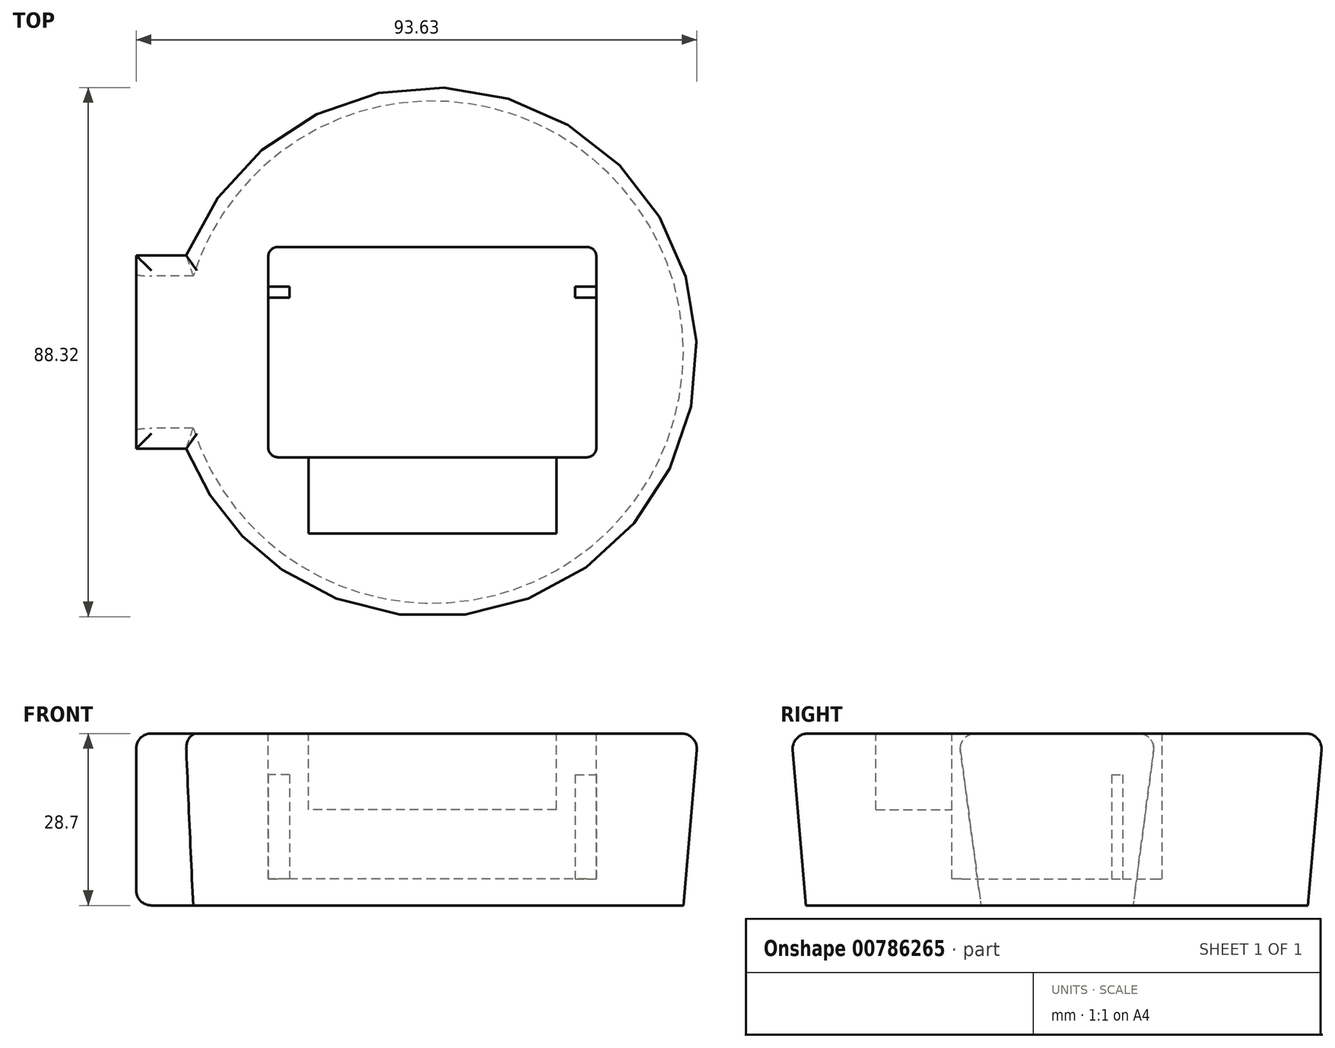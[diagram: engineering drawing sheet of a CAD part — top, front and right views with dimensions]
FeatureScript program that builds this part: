
annotation { "Feature Type Name" : "Feature", "Feature Type Description" : "" }
export const myFeature = defineFeature(function(context is Context, id is Id, definition is map)
    precondition{}
    {
        {
            var Q0;
            Q0=qCreatedBy(makeId("Front.planeOp"),FACE);
            var sketch = newSketch(context, id + "F0", { "sketchPlane" : qUnion([Q0])});
            skLineSegment(sketch, "E0", {"start": v(0, 0) * mm, "end": v(-41.91, 0) * mm});
            skLineSegment(sketch, "E1", {"start": v(-41.91, 0) * mm, "end": v(-44.39, 28.7) * mm});
            skLineSegment(sketch, "E2", {"start": v(-44.39, 28.7) * mm, "end": v(0, 28.7) * mm});
            skLineSegment(sketch, "E3", {"start": v(0, 28.7) * mm, "end": v(0, 0) * mm});
            skSolve(sketch);
        }
        {
            var Q0;
            Q0=makeQuery(id+"F0.imprint","IMPRINT",FACE,{"disambiguationData":[TD([[makeQuery(id+"F0.imprint","IMPRINT",EDGE,{"derivedFrom":sQuery(id+"F0.wireOp",EDGE,"E0")}),-1.0]])]});
            var sketch = newSketch(context, id + "F1", { "sketchPlane" : qUnion([Q0])});
            skLineSegment(sketch, "E4", {"start": v(0, -29.96) * mm, "end": v(0, 103.31) * mm, "construction": true});
            skSolve(sketch);
        }
        {
            var Q0;
            Q0 = qSketchRegion(id + "F0", true);
            var Q1;
            Q1=sQuery(id+"F1.wireOp",EDGE,"E4");
            revolve(context, id + "F2", {"surfaceOperationType" : NewSurfaceOperationType.NEW, "entities" : qUnion([Q0]), "axis" : qUnion([Q1]), "revolveType" : RevolveType.FULL});
        }
        {
            var Q0;
            Q0=makeQuery(id+"F2.opRevolve","SWEPT_FACE",FACE,{"disambiguationData":[OSD([sQuery(id+"F0.wireOp",EDGE,"E2")])]});
            var sketch = newSketch(context, id + "F3", { "sketchPlane" : qUnion([Q0])});
            skLineSegment(sketch, "E5.bottom", {"start": v(0, 16.51) * mm, "end": v(-49.47, 16.51) * mm});
            skLineSegment(sketch, "E5.top", {"start": v(0, -16.51) * mm, "end": v(-49.47, -16.51) * mm});
            skLineSegment(sketch, "E5.left", {"start": v(0, 16.51) * mm, "end": v(0, -16.51) * mm});
            skLineSegment(sketch, "E5.right", {"start": v(-49.47, 16.51) * mm, "end": v(-49.47, -16.51) * mm});
            skPoint(sketch, "E6", {"position": v(0, 0) * mm});
            skSolve(sketch);
        }
        {
            var Q0;
            Q0 = qSketchRegion(id + "F3", true);
            var Q1;
            Q1=makeQuery(id+"F2.opRevolve","SWEPT_FACE",FACE,{"disambiguationData":[OSD([sQuery(id+"F0.wireOp",EDGE,"E0")])]});
            extrude(context, id + "F4", {"entities" : qUnion([Q0]), "operationType" : NewBodyOperationType.ADD, "endBound" : BoundingType.UP_TO_SURFACE, "oppositeDirection" : true, "depth" : 25.4 * mm, "endBoundEntityFace" : qUnion([Q1]), "offsetDistance" : 25.4 * mm});
        }
        {
            var Q0;
            Q0=makeQuery(id+"F4.opExtrude","SWEPT_FACE",FACE,{"disambiguationData":[OSD([sQuery(id+"F3.wireOp",EDGE,"E5.right")])]});
            var sketch = newSketch(context, id + "F5", { "sketchPlane" : qUnion([Q0])});
            skLineSegment(sketch, "E7", {"start": v(-16.51, 28.7) * mm, "end": v(-16.51, 0) * mm});
            skLineSegment(sketch, "E8", {"start": v(-16.51, 0) * mm, "end": v(-12.7, 0) * mm});
            skLineSegment(sketch, "E9", {"start": v(-12.7, 0) * mm, "end": v(-16.51, 28.7) * mm});
            skLineSegment(sketch, "E10", {"start": v(16.5, 28.7) * mm, "end": v(16.5, 0) * mm});
            skLineSegment(sketch, "E11", {"start": v(16.5, 0) * mm, "end": v(12.7, 0) * mm});
            skLineSegment(sketch, "E12", {"start": v(12.7, 0) * mm, "end": v(16.5, 28.7) * mm});
            skSolve(sketch);
        }
        {
            var Q0;
            Q0 = qSketchRegion(id + "F5", true);
            var Q1;
            Q1=makeQuery(id+"F2.opRevolve","SWEPT_FACE",FACE,{"disambiguationData":[OSD([sQuery(id+"F0.wireOp",EDGE,"E1")])]});
            extrude(context, id + "F6", {"entities" : qUnion([Q0]), "operationType" : NewBodyOperationType.REMOVE, "endBound" : BoundingType.UP_TO_SURFACE, "oppositeDirection" : true, "depth" : 25.4 * mm, "endBoundEntityFace" : qUnion([Q1]), "offsetDistance" : 25.4 * mm});
        }
        {
            var Q0;
            Q0=makeQuery(id+"F4.boolean.opBoolean","MERGE",FACE,{"derivedFrom":[makeQuery(id+"F2.opRevolve","SWEPT_FACE",FACE,{"disambiguationData":[OSD([sQuery(id+"F0.wireOp",EDGE,"E2")])]}),makeQuery(id+"F4.opExtrude","CAP_FACE",FACE,{"disambiguationData":[OSD([sQuery(id+"F3.wireOp",EDGE,"E5.bottom"),sQuery(id+"F3.wireOp",EDGE,"E5.top"),sQuery(id+"F3.wireOp",EDGE,"E5.left"),sQuery(id+"F3.wireOp",EDGE,"E5.right")])],"isStart":true})]});
            var sketch = newSketch(context, id + "F7", { "sketchPlane" : qUnion([Q0])});
            skLineSegment(sketch, "E13.bottom", {"start": v(25.8, -17.55) * mm, "end": v(-25.8, -17.55) * mm});
            skLineSegment(sketch, "E13.top", {"start": v(25.8, 17.55) * mm, "end": v(-25.8, 17.55) * mm});
            skLineSegment(sketch, "E13.left", {"start": v(27.4, -15.96) * mm, "end": v(27.4, 15.96) * mm});
            skLineSegment(sketch, "E13.right", {"start": v(-27.4, -15.96) * mm, "end": v(-27.4, 15.96) * mm});
            skPoint(sketch, "E13.middle", {"position": v(0, 0) * mm});
            skPoint(sketch, "E14.visualSharp", {"position": v(-27.4, 17.55) * mm});
            skArc(sketch, "E14.filletArc", {"start": v(-25.8, 17.55) * mm, "mid": v(-26.93, 17.09) * mm, "end": v(-27.4, 15.96) * mm});
            skPoint(sketch, "E15.visualSharp", {"position": v(27.4, 17.55) * mm});
            skArc(sketch, "E15.filletArc", {"start": v(27.4, 15.96) * mm, "mid": v(26.93, 17.09) * mm, "end": v(25.8, 17.55) * mm});
            skPoint(sketch, "E16.visualSharp", {"position": v(27.4, -17.55) * mm});
            skArc(sketch, "E16.filletArc", {"start": v(25.8, -17.55) * mm, "mid": v(26.93, -17.09) * mm, "end": v(27.4, -15.96) * mm});
            skPoint(sketch, "E17.visualSharp", {"position": v(-27.4, -17.55) * mm});
            skArc(sketch, "E17.filletArc", {"start": v(-27.4, -15.96) * mm, "mid": v(-26.93, -17.09) * mm, "end": v(-25.8, -17.55) * mm});
            skSolve(sketch);
        }
        {
            var Q0;
            Q0 = qSketchRegion(id + "F7", true);
            extrude(context, id + "F8", {"entities" : qUnion([Q0]), "operationType" : NewBodyOperationType.REMOVE, "oppositeDirection" : true, "depth" : 24.28 * mm, "offsetDistance" : 25.4 * mm});
        }
        {
            var Q0;
            Q0=makeQuery(id+"F8.boolean.opBoolean","COPY",FACE,{"derivedFrom":makeQuery(id+"F8.opExtrude","CAP_FACE",FACE,{"disambiguationData":[OSD([sQuery(id+"F7.wireOp",EDGE,"E13.bottom"),sQuery(id+"F7.wireOp",EDGE,"E13.top"),sQuery(id+"F7.wireOp",EDGE,"E13.left"),sQuery(id+"F7.wireOp",EDGE,"E13.right"),sQuery(id+"F7.wireOp",EDGE,"E14.filletArc"),sQuery(id+"F7.wireOp",EDGE,"E15.filletArc"),sQuery(id+"F7.wireOp",EDGE,"E16.filletArc"),sQuery(id+"F7.wireOp",EDGE,"E17.filletArc")])],"isStart":false})});
            var sketch = newSketch(context, id + "F9", { "sketchPlane" : qUnion([Q0])});
            skLineSegment(sketch, "E18.bottom", {"start": v(23.84, 9.1) * mm, "end": v(27.4, 9.1) * mm});
            skLineSegment(sketch, "E18.top", {"start": v(23.84, 10.95) * mm, "end": v(27.4, 10.95) * mm});
            skLineSegment(sketch, "E18.left", {"start": v(23.84, 9.1) * mm, "end": v(23.84, 10.95) * mm});
            skLineSegment(sketch, "E18.right", {"start": v(27.4, 9.1) * mm, "end": v(27.4, 10.95) * mm});
            skPoint(sketch, "E18.middle", {"position": v(25.62, 10.02) * mm});
            skLineSegment(sketch, "E19.bottom", {"start": v(-23.84, 9.1) * mm, "end": v(-27.4, 9.1) * mm});
            skLineSegment(sketch, "E19.top", {"start": v(-23.84, 10.95) * mm, "end": v(-27.4, 10.95) * mm});
            skLineSegment(sketch, "E19.left", {"start": v(-23.84, 9.1) * mm, "end": v(-23.84, 10.95) * mm});
            skLineSegment(sketch, "E19.right", {"start": v(-27.4, 9.1) * mm, "end": v(-27.4, 10.95) * mm});
            skPoint(sketch, "E19.middle", {"position": v(-25.62, 10.02) * mm});
            skSolve(sketch);
        }
        {
            var Q0;
            Q0 = qSketchRegion(id + "F9", true);
            extrude(context, id + "F10", {"entities" : qUnion([Q0]), "operationType" : NewBodyOperationType.ADD, "depth" : 17.42 * mm, "offsetDistance" : 25.4 * mm});
        }
        {
            var Q0;
            Q0=makeQuery(id+"F4.boolean.opBoolean","MERGE",FACE,{"derivedFrom":[makeQuery(id+"F2.opRevolve","SWEPT_FACE",FACE,{"disambiguationData":[OSD([sQuery(id+"F0.wireOp",EDGE,"E2")])]}),makeQuery(id+"F4.opExtrude","CAP_FACE",FACE,{"disambiguationData":[OSD([sQuery(id+"F3.wireOp",EDGE,"E5.bottom"),sQuery(id+"F3.wireOp",EDGE,"E5.top"),sQuery(id+"F3.wireOp",EDGE,"E5.left"),sQuery(id+"F3.wireOp",EDGE,"E5.right")])],"isStart":true})]});
            var sketch = newSketch(context, id + "F11", { "sketchPlane" : qUnion([Q0])});
            skLineSegment(sketch, "E20.bottom", {"start": v(20.7, -30.25) * mm, "end": v(-20.7, -30.25) * mm});
            skLineSegment(sketch, "E20.top", {"start": v(20.7, -17.55) * mm, "end": v(-20.7, -17.55) * mm});
            skLineSegment(sketch, "E20.left", {"start": v(20.7, -30.25) * mm, "end": v(20.7, -17.55) * mm});
            skLineSegment(sketch, "E20.right", {"start": v(-20.7, -30.25) * mm, "end": v(-20.7, -17.55) * mm});
            skPoint(sketch, "E20.middle", {"position": v(0, -23.9) * mm});
            skSolve(sketch);
        }
        {
            var Q0;
            Q0 = qSketchRegion(id + "F11", true);
            extrude(context, id + "F12", {"entities" : qUnion([Q0]), "operationType" : NewBodyOperationType.REMOVE, "oppositeDirection" : true, "depth" : 12.7 * mm, "offsetDistance" : 25.4 * mm});
        }
        {
            var Q0;
            Q0=makeQuery(id+"F2.opRevolve","SWEPT_EDGE",EDGE,{"disambiguationData":[OSD([sQuery(id+"F0.wireOp",EDGE,"E1"),sQuery(id+"F0.wireOp",EDGE,"E2")])]});
            var Q1;
            Q1=makeQuery(id+"F6.boolean.opBoolean","MERGE",EDGE,{"derivedFrom":[makeQuery(id+"F4.opExtrude","CAP_EDGE",EDGE,{"disambiguationData":[OSD([sQuery(id+"F3.wireOp",EDGE,"E5.top")])],"isStart":true})],"fromTools":[makeQuery(id+"F6.opExtrude","SWEPT_EDGE",EDGE,{"disambiguationData":[OSD([sQuery(id+"F3.wireOp",EDGE,"E5.right"),sQuery(id+"F5.wireOp",EDGE,"E10"),sQuery(id+"F5.wireOp",EDGE,"E12")])]})]});
            var Q2;
            Q2=makeQuery(id+"F4.opExtrude","CAP_EDGE",EDGE,{"disambiguationData":[OSD([sQuery(id+"F3.wireOp",EDGE,"E5.right")])],"isStart":true});
            var Q3;
            Q3=makeQuery(id+"F6.boolean.opBoolean","MERGE",EDGE,{"derivedFrom":[makeQuery(id+"F4.opExtrude","CAP_EDGE",EDGE,{"disambiguationData":[OSD([sQuery(id+"F3.wireOp",EDGE,"E5.bottom")])],"isStart":true})],"fromTools":[makeQuery(id+"F6.opExtrude","SWEPT_EDGE",EDGE,{"disambiguationData":[OSD([sQuery(id+"F3.wireOp",EDGE,"E5.right"),sQuery(id+"F5.wireOp",EDGE,"E7"),sQuery(id+"F5.wireOp",EDGE,"E9")])]})]});
            var Q4;
            Q4=makeQuery(id+"F6.boolean.opBoolean","COPY",EDGE,{"derivedFrom":makeQuery(id+"F6.opExtrude","CAP_EDGE",EDGE,{"disambiguationData":[OSD([sQuery(id+"F5.wireOp",EDGE,"E12")])],"isStart":true})});
            var Q5;
            Q5=makeQuery(id+"F6.boolean.opBoolean","COPY",EDGE,{"derivedFrom":makeQuery(id+"F6.opExtrude","SWEPT_EDGE",EDGE,{"disambiguationData":[OSD([sQuery(id+"F3.wireOp",EDGE,"E5.right"),sQuery(id+"F5.wireOp",EDGE,"E11"),sQuery(id+"F5.wireOp",EDGE,"E12")])]})});
            var Q6;
            Q6=makeQuery(id+"F6.boolean.opBoolean","MERGE",EDGE,{"derivedFrom":[makeQuery(id+"F2.opRevolve","SWEPT_EDGE",EDGE,{"disambiguationData":[OSD([sQuery(id+"F0.wireOp",EDGE,"E0"),sQuery(id+"F0.wireOp",EDGE,"E1")])]})],"fromTools":[makeQuery(id+"F6.opExtrude","CAP_EDGE",EDGE,{"disambiguationData":[OSD([sQuery(id+"F5.wireOp",EDGE,"E8")])],"isStart":false}),makeQuery(id+"F6.opExtrude","CAP_EDGE",EDGE,{"disambiguationData":[OSD([sQuery(id+"F5.wireOp",EDGE,"E11")])],"isStart":false})]});
            var Q7;
            Q7=makeQuery(id+"F6.boolean.opBoolean","COPY",EDGE,{"derivedFrom":makeQuery(id+"F6.opExtrude","SWEPT_EDGE",EDGE,{"disambiguationData":[OSD([sQuery(id+"F3.wireOp",EDGE,"E5.right"),sQuery(id+"F5.wireOp",EDGE,"E8"),sQuery(id+"F5.wireOp",EDGE,"E9")])]})});
            var Q8;
            Q8=makeQuery(id+"F6.boolean.opBoolean","COPY",EDGE,{"derivedFrom":makeQuery(id+"F6.opExtrude","CAP_EDGE",EDGE,{"disambiguationData":[OSD([sQuery(id+"F5.wireOp",EDGE,"E9")])],"isStart":true})});
            var Q9;
            Q9=makeQuery(id+"F4.opExtrude","CAP_EDGE",EDGE,{"disambiguationData":[OSD([sQuery(id+"F3.wireOp",EDGE,"E5.right")])],"isStart":false});
            var Q10;
            Q10=makeQuery(id+"F8.boolean.opBoolean","COPY",EDGE,{"derivedFrom":makeQuery(id+"F8.opExtrude","CAP_EDGE",EDGE,{"disambiguationData":[OSD([sQuery(id+"F7.wireOp",EDGE,"E13.top")])],"isStart":true})});
            var Q11;
            Q11=makeQuery(id+"F12.boolean.opBoolean","COPY",EDGE,{"derivedFrom":makeQuery(id+"F12.opExtrude","CAP_EDGE",EDGE,{"disambiguationData":[OSD([sQuery(id+"F11.wireOp",EDGE,"E20.top")])],"isStart":false})});
            var Q12;
            Q12=makeQuery(id+"F12.boolean.opBoolean","COPY",EDGE,{"derivedFrom":makeQuery(id+"F12.opExtrude","CAP_EDGE",EDGE,{"disambiguationData":[OSD([sQuery(id+"F11.wireOp",EDGE,"E20.bottom")])],"isStart":true})});
            var Q13;
            Q13=makeQuery(id+"F12.boolean.opBoolean","COPY",EDGE,{"derivedFrom":makeQuery(id+"F12.opExtrude","SWEPT_EDGE",EDGE,{"disambiguationData":[OSD([sQuery(id+"F7.wireOp",EDGE,"E13.bottom"),sQuery(id+"F11.wireOp",EDGE,"E20.top"),sQuery(id+"F11.wireOp",EDGE,"E20.right")])]})});
            var Q14;
            Q14=makeQuery(id+"F12.boolean.opBoolean","COPY",EDGE,{"derivedFrom":makeQuery(id+"F12.opExtrude","CAP_EDGE",EDGE,{"disambiguationData":[OSD([sQuery(id+"F11.wireOp",EDGE,"E20.right")])],"isStart":true})});
            var Q15;
            Q15=makeQuery(id+"F12.boolean.opBoolean","COPY",EDGE,{"derivedFrom":makeQuery(id+"F12.opExtrude","CAP_EDGE",EDGE,{"disambiguationData":[OSD([sQuery(id+"F11.wireOp",EDGE,"E20.left")])],"isStart":true})});
            var Q16;
            Q16=makeQuery(id+"F12.boolean.opBoolean","COPY",EDGE,{"derivedFrom":makeQuery(id+"F12.opExtrude","SWEPT_EDGE",EDGE,{"disambiguationData":[OSD([sQuery(id+"F7.wireOp",EDGE,"E13.bottom"),sQuery(id+"F11.wireOp",EDGE,"E20.top"),sQuery(id+"F11.wireOp",EDGE,"E20.left")])]})});
            fillet(context, id + "F13", {"entities" : qUnion([Q0, Q1, Q2, Q3, Q4, Q5, Q6, Q7, Q8, Q9, Q10, Q11, Q12, Q13, Q14, Q15, Q16]), "radius" : 2.54 * mm, "tangentPropagation" : true, "allowEdgeOverflow" : false});
        }
    });
